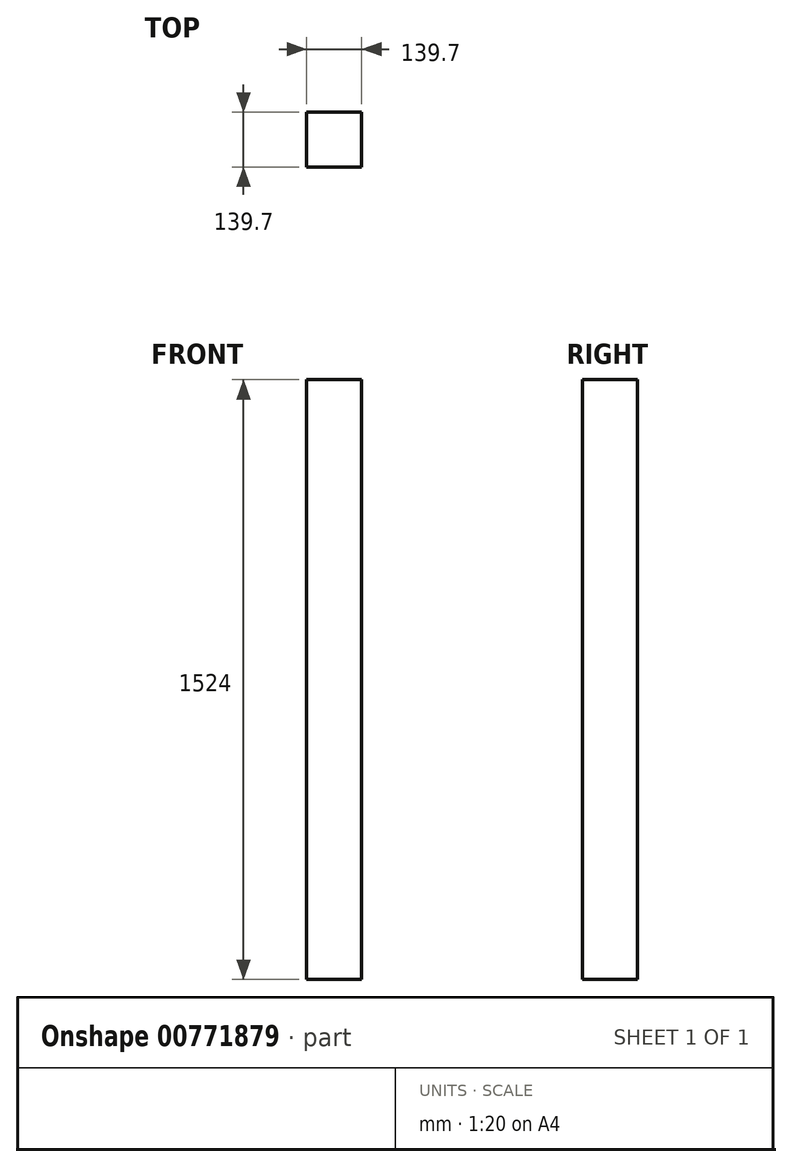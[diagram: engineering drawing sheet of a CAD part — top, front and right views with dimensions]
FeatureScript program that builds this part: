
annotation { "Feature Type Name" : "Feature", "Feature Type Description" : "" }
export const myFeature = defineFeature(function(context is Context, id is Id, definition is map)
    precondition{}
    {
        {
            var Q0;
            Q0=qCreatedBy(makeId("Top.planeOp"),FACE);
            var sketch = newSketch(context, id + "F0", { "sketchPlane" : qUnion([Q0])});
            skLineSegment(sketch, "E0.bottom", {"start": v(69.85, 69.85) * mm, "end": v(-69.85, 69.85) * mm});
            skLineSegment(sketch, "E0.top", {"start": v(69.85, -69.85) * mm, "end": v(-69.85, -69.85) * mm});
            skLineSegment(sketch, "E0.left", {"start": v(69.85, 69.85) * mm, "end": v(69.85, -69.85) * mm});
            skLineSegment(sketch, "E0.right", {"start": v(-69.85, 69.85) * mm, "end": v(-69.85, -69.85) * mm});
            skPoint(sketch, "E0.middle", {"position": v(0, 0) * mm});
            skSolve(sketch);
        }
        {
            var Q0;
            Q0 = qSketchRegion(id + "F0", true);
            extrude(context, id + "F1", {"entities" : qUnion([Q0]), "depth" : 1524 * mm, "offsetDistance" : 25.4 * mm});
        }
    });
